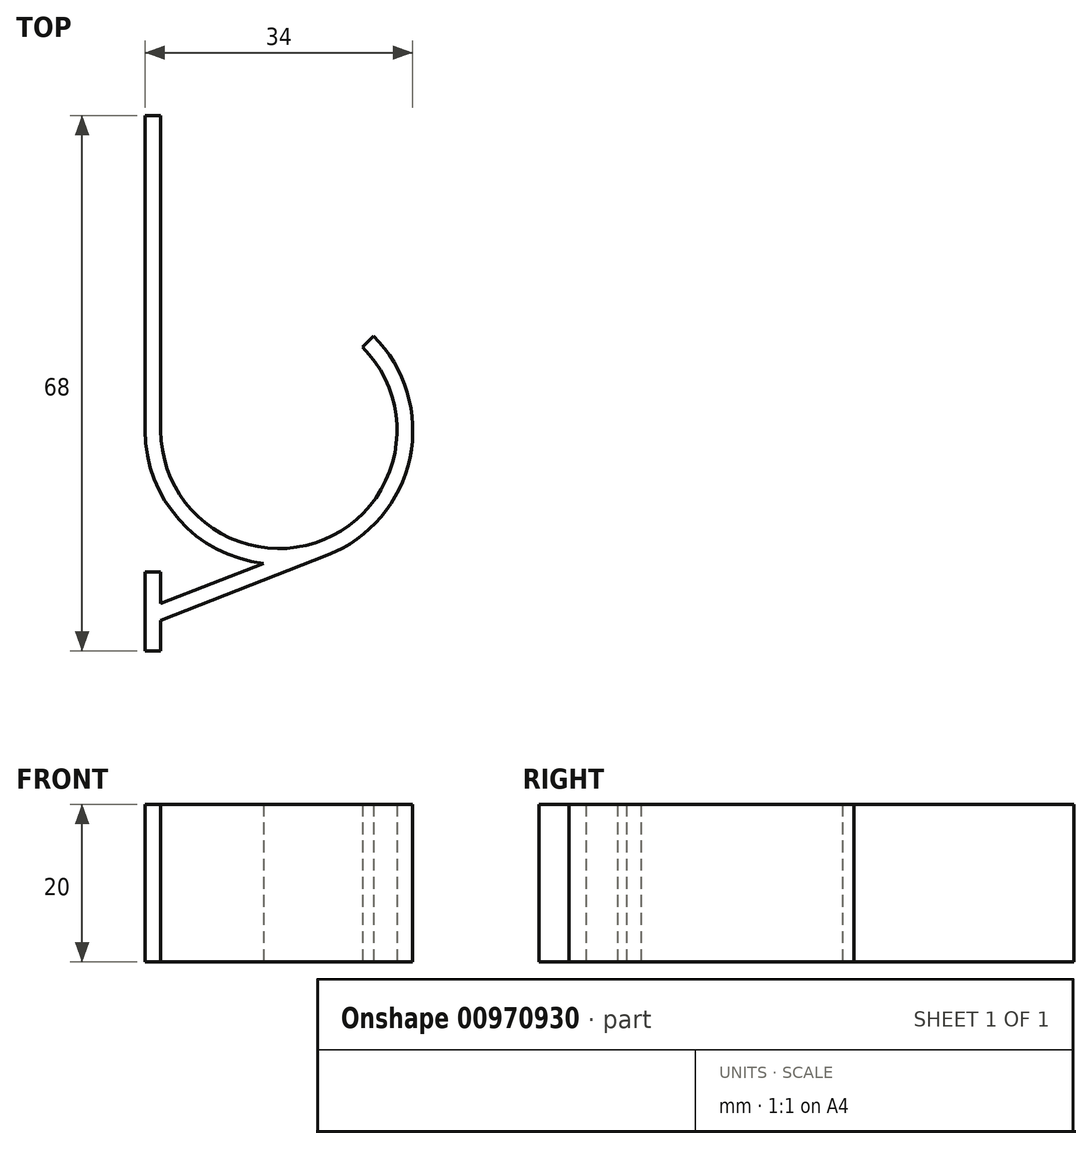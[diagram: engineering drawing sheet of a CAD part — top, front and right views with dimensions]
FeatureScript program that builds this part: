
annotation { "Feature Type Name" : "Feature", "Feature Type Description" : "" }
export const myFeature = defineFeature(function(context is Context, id is Id, definition is map)
    precondition{}
    {
        {
            var Q0;
            Q0=qCreatedBy(makeId("Top.planeOp"),FACE);
            var sketch = newSketch(context, id + "F0", { "sketchPlane" : qUnion([Q0])});
            skLineSegment(sketch, "E0", {"start": v(-29.77, 51.1) * mm, "end": v(-29.77, 11.1) * mm});
            skLineSegment(sketch, "E1", {"start": v(-29.77, 11.1) * mm, "end": v(-14.77, 11.1) * mm, "construction": true});
            skCircle(sketch, "E2", {"center": v(-14.77, 11.1) * mm, "radius": 15 * mm});
            skLineSegment(sketch, "E3", {"start": v(-14.77, 11.1) * mm, "end": v(-2.75, 23.12) * mm});
            skCircle(sketch, "E4.0", {"center": v(-14.77, 11.1) * mm, "radius": 17 * mm});
            skLineSegment(sketch, "E5.0", {"start": v(-31.77, 51.1) * mm, "end": v(-31.77, 11.1) * mm});
            skLineSegment(sketch, "E6", {"start": v(-29.77, 51.1) * mm, "end": v(-31.77, 51.1) * mm});
            skLineSegment(sketch, "E7", {"start": v(-8.56, -4.72) * mm, "end": v(-29.77, -13.04) * mm});
            skLineSegment(sketch, "E8", {"start": v(-9.3, -2.86) * mm, "end": v(-29.77, -10.9) * mm});
            skLineSegment(sketch, "E9", {"start": v(-29.77, 11.1) * mm, "end": v(-31.77, 11.1) * mm, "construction": true});
            skLineSegment(sketch, "E10", {"start": v(-29.77, -6.9) * mm, "end": v(-29.77, -16.9) * mm});
            skLineSegment(sketch, "E11", {"start": v(-31.77, -6.9) * mm, "end": v(-31.77, -16.9) * mm});
            skLineSegment(sketch, "E12", {"start": v(-29.77, -6.9) * mm, "end": v(-31.77, -6.9) * mm});
            skLineSegment(sketch, "E13", {"start": v(-31.77, -16.9) * mm, "end": v(-29.77, -16.9) * mm});
            skLineSegment(sketch, "E14", {"start": v(-31.77, 11.1) * mm, "end": v(-31.77, -6.9) * mm, "construction": true});
            skSolve(sketch);
        }
        {
            var Q0;
            {var subQ4=sQuery(id+"F0.wireOp",EDGE,"E5.0");Q0=makeQuery(id+"F0.imprint","IMPRINT",FACE,{"disambiguationData":[TD([[makeQuery(id+"F0.imprint","IMPRINT",EDGE,{"derivedFrom":subQ4}),1.0]])]});}
            var Q1;
            {var subQ3=sQuery(id+"F0.wireOp",EDGE,"E2");var subQ5=sQuery(id+"F0.wireOp",EDGE,"E0");var subQ6=makeQuery(id+"F0.imprint","INTERSECT",VERTEX,{"derivedFrom":[subQ5,subQ3]});Q1=makeQuery(id+"F0.imprint","IMPRINT",FACE,{"disambiguationData":[TD([[makeQuery(id+"F0.imprint","IMPRINT",EDGE,{"disambiguationData":[TD([[subQ6,1.0]])],"derivedFrom":subQ5}),-1.0]])]});}
            var Q2;
            {var subQ4=sQuery(id+"F0.wireOp",EDGE,"E2");var subQ6=sQuery(id+"F0.wireOp",EDGE,"E8");var subQ8=makeQuery(id+"F0.imprint","INTERSECT",VERTEX,{"derivedFrom":[subQ4,subQ6]});Q2=makeQuery(id+"F0.imprint","IMPRINT",FACE,{"disambiguationData":[TD([[makeQuery(id+"F0.imprint","IMPRINT",EDGE,{"disambiguationData":[TD([[subQ8,-1.0]])],"derivedFrom":subQ4}),-1.0]])]});}
            var Q3;
            {var subQ0=sQuery(id+"F0.wireOp",EDGE,"E7");Q3=makeQuery(id+"F0.imprint","IMPRINT",FACE,{"disambiguationData":[TD([[makeQuery(id+"F0.imprint","IMPRINT",EDGE,{"derivedFrom":subQ0}),-1.0]])]});}
            var Q4;
            Q4=makeQuery(id+"F0.imprint","IMPRINT",FACE,{"disambiguationData":[TD([[makeQuery(id+"F0.imprint","IMPRINT",EDGE,{"derivedFrom":sQuery(id+"F0.wireOp",EDGE,"E11")}),1.0]])]});
            extrude(context, id + "F1", {"entities" : qUnion([Q0, Q1, Q2, Q3, Q4]), "depth" : 20 * mm, "offsetDistance" : 25 * mm});
        }
    });
